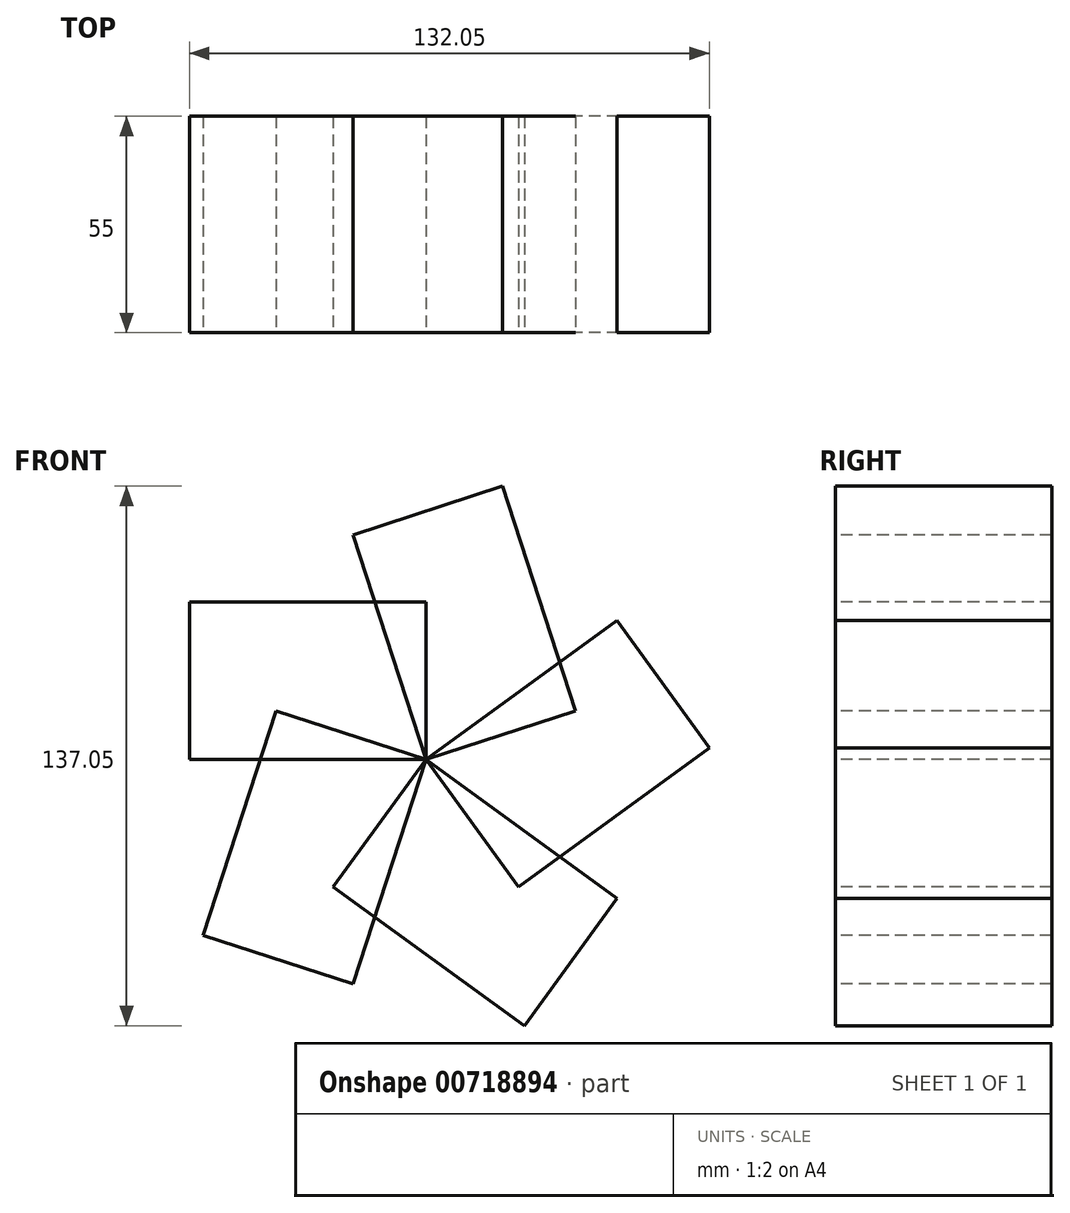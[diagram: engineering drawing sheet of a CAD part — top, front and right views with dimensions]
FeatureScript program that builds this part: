
annotation { "Feature Type Name" : "Feature", "Feature Type Description" : "" }
export const myFeature = defineFeature(function(context is Context, id is Id, definition is map)
    precondition{}
    {
        {
            var Q0;
            Q0=qCreatedBy(makeId("Top.planeOp"),FACE);
            var sketch = newSketch(context, id + "F0", { "sketchPlane" : qUnion([Q0])});
            skLineSegment(sketch, "E0.bottom", {"start": v(-60, 55) * mm, "end": v(0, 55) * mm});
            skLineSegment(sketch, "E0.top", {"start": v(-60, 0) * mm, "end": v(0, 0) * mm});
            skLineSegment(sketch, "E0.left", {"start": v(-60, 55) * mm, "end": v(-60, 0) * mm});
            skLineSegment(sketch, "E0.right", {"start": v(0, 55) * mm, "end": v(0, 0) * mm});
            skSolve(sketch);
        }
        {
            var Q0;
            Q0 = qSketchRegion(id + "F0", true);
            extrude(context, id + "F1", {"entities" : qUnion([Q0]), "depth" : 40 * mm, "offsetDistance" : 25 * mm});
        }
        {
            var Q0;
            Q0=makeQuery(id+"F1.opExtrude","SWEPT_BODY",BODY,{"disambiguationData":[OSD([sQuery(id+"F0.wireOp",EDGE,"E0.bottom"),sQuery(id+"F0.wireOp",EDGE,"E0.top"),sQuery(id+"F0.wireOp",EDGE,"E0.left"),sQuery(id+"F0.wireOp",EDGE,"E0.right")])]});
            var Q1;
            Q1=makeQuery(id+"F1.opExtrude","CAP_EDGE",EDGE,{"disambiguationData":[OSD([sQuery(id+"F0.wireOp",EDGE,"E0.right")])],"isStart":true});
            circularPattern(context, id + "F2", {"entities" : qUnion([Q0]), "axis" : qUnion([Q1]), "angle" : 360 * degree, "instanceCount" : 5, "equalSpace" : true});
        }
    });
